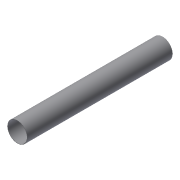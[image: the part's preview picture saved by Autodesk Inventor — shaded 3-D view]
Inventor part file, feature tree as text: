
AUTODESK INVENTOR PART (.ipt)
format: ipt  version: 2016 (Build 200138000, 138)  size: 73,728 bytes
history: native  units: in
note: dims shown in document units (in); Inventor stores cm internally (conversion verified against a paired STEP export)
features: extrude x1, sketch x1
ambient origin geometry x8: Origin, YZ Plane, XZ Plane, XY Plane, X Axis, Y Axis, Z Axis, Center Point
bodies: Solid1 (feature_tree)
feature tree (2):
  extrude  "Extrusion1"  Depth=31.4016in TaperAngle=0.0deg
  sketch  "Sketch1"  dims[d1=0.0906in d2=31.4016in d3=0.0in d4=4.3307in]
